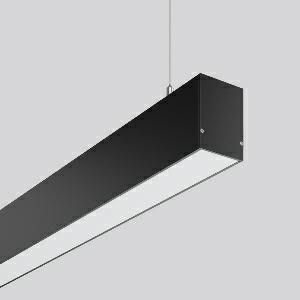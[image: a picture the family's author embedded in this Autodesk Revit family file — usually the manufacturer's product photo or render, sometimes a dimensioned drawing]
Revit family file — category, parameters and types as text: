
# Revit family: less_is_more_50_312311_003_76_16bf
name_source: partatom
category: Lighting Fixtures
units: mm (PartAtom-declared; Revit-internal decimal feet)

## family parameters
Cut with Voids When Loaded = No
Host = Face
Light Source = No
Part Type = Normal
Room Calculation Point = No
Round Connector Dimension = Use Diameter
Shared = No

## types (1)
- LESS IS MORE 50 (1 x LED Modul 830, 2300 lm, 3000)
    Apparent Load = 22 VA
    CIE Flux Codes = 48 79 95 100 100
    Color Rendering = 80
    Color Temperature = 3000
    Default Elevation = 1800 mm
    Description = Series: LESS IS MORE 50
Linear pendant luminaire for aesthetically sophisticated lighting. Housing: extruded aluminium profile, powder-coated. End cap aluminium powder-coated. Canopy made of aluminium, powder-coated. Diffuser made of non-yellowing plastic (PMMA), opal. Direct light emission. Suitable for pendant. 2-point steel cable suspension freely positionable and infinitely height-adjustable. Special lengths available on request. LED unit with integrated converter interchangeable and removable. Suitable for through-wiring. With sensors or as a safety luminaire on request. 
Colour: deep black, matt (RAL 9005)
Length: 847 mm
Width: 57 mm
Height: 75 mm
Suspension length: 2000 mm
Lamp: LED
Socket: without socket
Colour temperature: 3000K
Colour rendering index (CRI): 80
System power: 22 W
Rated luminous flux: 2300 lm
Luminous efficiency: 105 lm/W
Control gear: Converter, dimmable, DALI
Protection class: I
Type of protection: IP 20
    Height = 75 mm
    Lamp = 1 x LED Modul 830
    Lamp Light Flux = 2300 lm
    Lamp count = 1
    Length = 847 mm
    Lifetime = 50000 h
    Luminous efficacy = 105 lm/W
    Manufacturer = RZB
    ModVariant = No
    Model = 312311.003.76
    Mounting Place = Ceiling
    Mounting Type = Pendant
    Number of Poles = 1
    OnlyDefault = Yes
    Power Factor = 1
    Product Name = LESS IS MORE 50
    Product group = Pendant LED linear luminaires
    ProductGroupID = 907
    Protection Class = Protection class I
    Protection Degree = IP 20
    RLX_Detail_Level = 1
    RLX_Emergency_Light_Flux = 0 lm
    RLX_Emergency_Type = 0
    RLX_Emergency_Type_DB = No
    RlxData = <blob elided: 28869 chars, md5=92a060d8>
    Socket = socket
    Standby Power = 0 W
    System Light Flux = 2300 lm
    System Power = 22 W
    Type Comments = Product without accessories
    Type Image = 312318.003.jpg
    URL = http://relux.com
    VarID = ---
    Voltage = 230 V
    Voltage Range = 220-240 V
    Weight = 0.00 kg
    Width = 57 mm

## geometry (parser evidence)
native form markers: Blend x4, Sweep x9
no freeform markers — native parametric forms only
